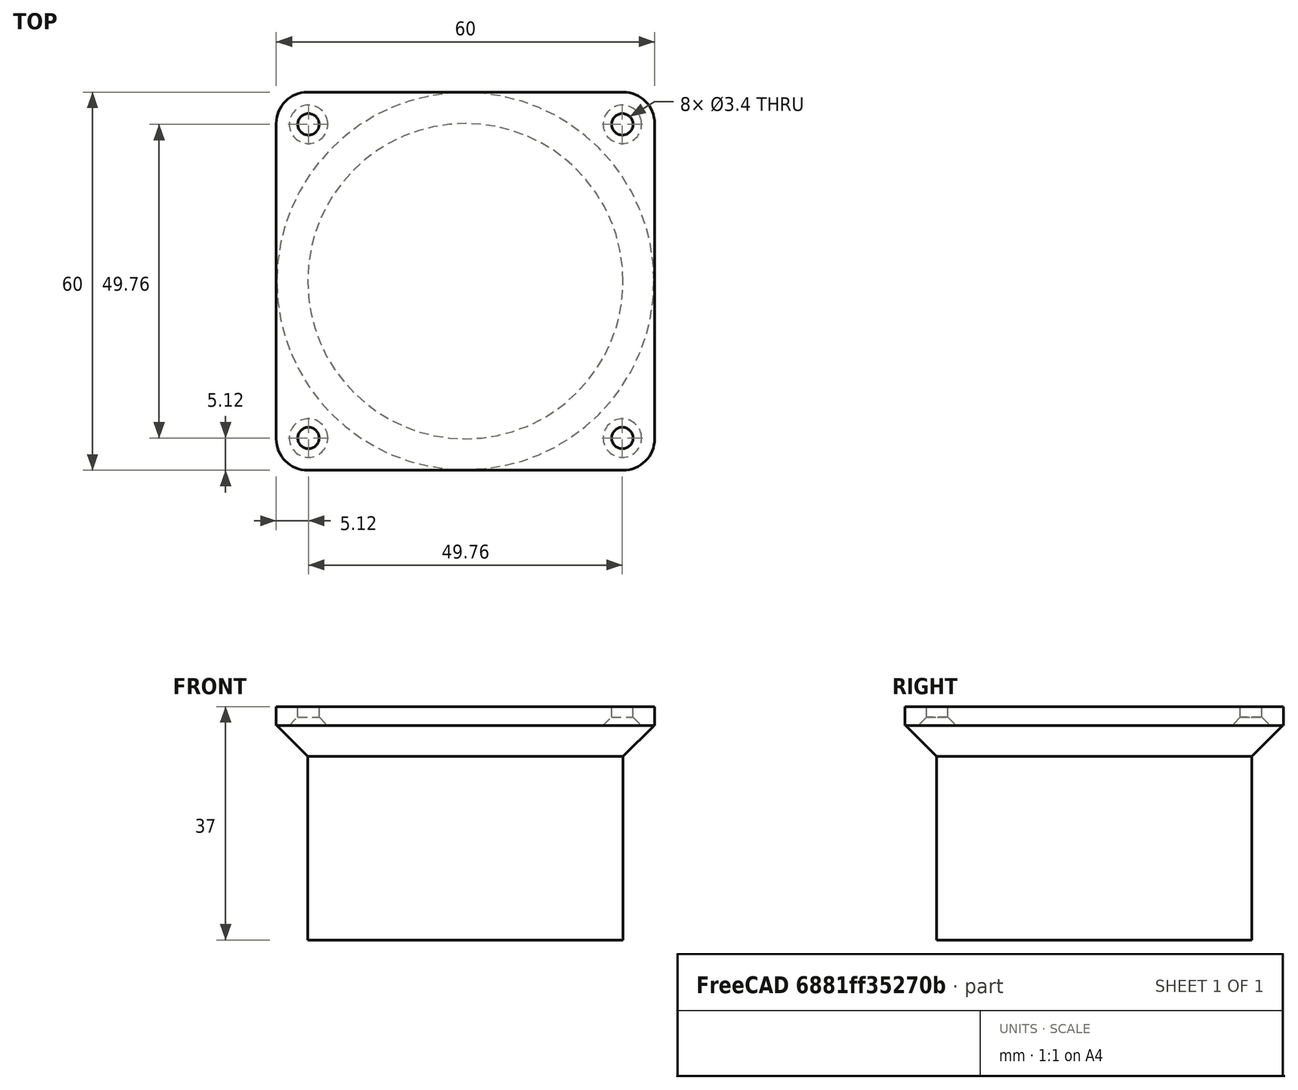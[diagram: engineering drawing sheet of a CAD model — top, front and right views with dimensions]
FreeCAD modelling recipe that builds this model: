
FCSTD DOCUMENT  (FreeCAD 0.19R24267 +99 (Git))
Label: patas_estante
License: All rights reserved
LicenseURL: http://en.wikipedia.org/wiki/All_rights_reserved
objects: Sketcher::SketchObject×2, Part::Cylinder×1, PartDesign::Pad×1, PartDesign::Hole×1, PartDesign::Body×1, Part::MultiFuse×1, Part::Chamfer×1, Mesh::Feature×1
note: 10 computed .brp shape members not serialized (recipe doc carries the construction recipe); baked Part::Feature solids carry a one-line shape summary decoded from their .brp

FEATURE [Part::Cylinder] Cylinder
  Angle = 360
  AttacherType = Attacher::AttachEngine3D
  Height = 37
  Placement = pos=(0,0,-34) rot=(0,0,1;0rad)
  Radius = 25
FEATURE [Sketcher::SketchObject] Sketch
  FullyConstrained = true
  MapMode = 5
  Support = -> [XY_Plane]
  sketch-geometry (8):
    g0: LineSegment StartX=-25 StartY=30 StartZ=0 EndX=25 EndY=30 EndZ=0
    g1: LineSegment StartX=30 StartY=25 StartZ=0 EndX=30 EndY=-25 EndZ=0
    g2: LineSegment StartX=25 StartY=-30 StartZ=0 EndX=-25 EndY=-30 EndZ=0
    g3: LineSegment StartX=-30 StartY=-25 StartZ=0 EndX=-30 EndY=25 EndZ=0
    g4: ArcOfCircle CenterX=-25 CenterY=25 CenterZ=0 NormalX=0 NormalY=0 NormalZ=1 AngleXU=0 Radius=5 StartAngle=1.5708 EndAngle=3.14159
    g5: ArcOfCircle CenterX=-25 CenterY=-25 CenterZ=0 NormalX=0 NormalY=0 NormalZ=1 AngleXU=0 Radius=5 StartAngle=3.14159 EndAngle=4.71239
    g6: ArcOfCircle CenterX=25 CenterY=-25 CenterZ=0 NormalX=0 NormalY=0 NormalZ=1 AngleXU=0 Radius=5 StartAngle=4.71239 EndAngle=6.28319
    g7: ArcOfCircle CenterX=25 CenterY=25 CenterZ=0 NormalX=0 NormalY=0 NormalZ=1 AngleXU=0 Radius=5 StartAngle=0 EndAngle=1.5708
  constraints (19):
    c: Horizontal(g0)
    c: Horizontal(g2)
    c: Vertical(g1)
    c: Vertical(g3)
    c: Equal(g3,g0)
    c: Tangent(g0,g4) = 1.5708
    c: Tangent(g3,g4) = 1.5708
    c: Tangent(g3,g5) = 1.5708
    c: Tangent(g2,g5) = 1.5708
    c: Tangent(g2,g6) = 1.5708
    c: Tangent(g1,g6) = 1.5708
    c: Tangent(g1,g7) = 1.5708
    c: Tangent(g0,g7) = 1.5708
    c: Equal(g4,g7)
    c: Equal(g7,g5)
    c: Equal(g5,g6)
    c: Radius(g4) = 5
    c: Symmetric(g4,g6,g-1)
    c: DistanceX(g3,g1) = 60
FEATURE [PartDesign::Pad] Pad
  Direction = (1,1,1)
  Length = 3
  Length2 = 100
  Profile = -> Sketch
  Type = 0
FEATURE [Sketcher::SketchObject] Sketch001
  FullyConstrained = true
  MapMode = 5
  Placement = pos=(0,0,0) rot=(1,0,0;3.14159rad)
  Support = -> [Pad]
  sketch-geometry (4):
    g0: Circle CenterX=-24.88 CenterY=-24.88 CenterZ=0 NormalX=0 NormalY=0 NormalZ=1 AngleXU=0 Radius=1.5
    g1: Circle CenterX=24.88 CenterY=-24.88 CenterZ=0 NormalX=0 NormalY=0 NormalZ=1 AngleXU=0 Radius=1.5
    g2: Circle CenterX=24.88 CenterY=24.88 CenterZ=0 NormalX=0 NormalY=0 NormalZ=1 AngleXU=0 Radius=1.5
    g3: Circle CenterX=-24.88 CenterY=24.88 CenterZ=0 NormalX=0 NormalY=0 NormalZ=1 AngleXU=0 Radius=1.5
  constraints (10):
    c: Equal(g0,g1)
    c: DistanceY(g-1,g2) = 24.88
    c: Radius(g2) = 1.5
    c: Symmetric(g2,g0,g-1)
    c: Symmetric(g1,g3,g-1)
    c: Equal(g1,g2)
    c: Equal(g2,g3)
    c: DistanceX(g-1,g2) = 24.88
    c: Vertical(g1,g2)
    c: Horizontal(g3,g2)
FEATURE [PartDesign::Hole] Hole
  BaseFeature = -> Pad
  Depth = 25
  DepthType = 0
  Diameter = 3.4
  DrillForDepth = false
  DrillPoint = 1
  DrillPointAngle = 118
  HoleCutCountersinkAngle = 90
  HoleCutCustomValues = false
  HoleCutDepth = 3.4
  HoleCutDiameter = 6.1
  HoleCutType = 2
  ModelActualThread = false
  Profile = -> Sketch001
  Tapered = false
  TaperedAngle = 90
  ThreadAngle = 0
  ThreadClass = 0
  ThreadCutOffInner = 0
  ThreadCutOffOuter = 0
  ThreadDirection = 0
  ThreadFit = 0
  ThreadPitch = 0
  ThreadSize = 9
  ThreadType = 1
  Threaded = false
FEATURE [PartDesign::Body] Body
  Group = -> [Sketch,Pad,Sketch001,Hole]
  Origin = -> Origin
  Tip = -> Hole
FEATURE [Part::MultiFuse] Fusion
  Shapes = -> [Hole,Cylinder]
FEATURE [Part::Chamfer] Chamfer  label="pata_35"
  Base = -> Fusion
  Edges = 1 edges r=4.9: [Edge17]
FEATURE [Mesh::Feature] Mesh  label="pata_35 (Meshed)"
